# Revit family: Комби-клапан – регулятор расхода 4006_R
name_source: partatom
category: Rohrzubehör
revit_build: Autodesk Revit 2018 (Build: 20190510_1515(x64)
units: mm (PartAtom-declared; Revit-internal decimal feet)

## family parameters
Arbeitsebenenbasiert = Nein
Beim Laden mit Abzugskörper schneiden = Nein
Bemaßung runder Anschluss = Durchmesser verwenden
Gemeinsam genutzt = Nein
Immer vertikal = Ja
OmniClass-Nummer = 23.65.55.14
OmniClass-Titel = Valves for Liquid Services
Teiletyp = Unterbricht

## types (1)
- Комби-клапан – регулятор расхода 4006_R
    H05 = 9 mm  [stored 0.0295276 ft]
    H07 = 4 mm  [stored 0.0131234 ft]
    H09 = 21.8 mm  [stored 0.0715223 ft]
    H12 = 19.25 mm  [stored 0.0631562 ft]
    Hersteller = Herz-Armaturen GmbH
    L02 = 43.5 mm  [stored 0.142717 ft]
    L03 = 3.2 mm  [stored 0.0104987 ft]
    L04 = 1.5 mm  [stored 0.00492126 ft]
    L05 = 11 mm  [stored 0.0360892 ft]
    PN = 16
    R04 = 12.5 mm  [stored 0.0410105 ft]
    R05 = 15 mm  [stored 0.0492126 ft]
    R08 = 11.3 mm  [stored 0.0370735 ft]
    R09 = 18.25 mm  [stored 0.0598753 ft]
    R10 = 35 mm  [stored 0.114829 ft]
    R11 = 6.5 mm
    R12 = 3.9 mm  [stored 0.0127953 ft]
    SCRNCODE = 05;04;02
    SCRNSEQ = ARM;ARM_TYP="DURR";2
    URL = www.herz-armaturen.ru
    VRL02 = 18 mm  [stored 0.0590551 ft]
    VRL04 = 8 mm  [stored 0.0262467 ft]
    Защитный колпачок = Пластик
    Импульсная трубка = Медь Cu-DHP (CW024A)
    Кольцевое уплотнение O-Ring = EPDM
    Корпус = Латунь, устойчивая к селективной цинковой коррозии
    Корпус мембраны = латунь CW602N
    Макс. рабочая температура до DN32 = 130 °C
    Макс. рабочая температура от DN40 = 110 °C
    Макс. рабочее давление = 1600000.0 Pa
    Мембрана = EPDM
    Мин. рабочая температура (антифриз) = -20 °C
    Мин. рабочая температура (чистая вода) = 2 °C
    Область применения = Комби-клапан применяется в системах отопления и охлаждения с насосами. Комби-клапан автоматически ограничивает расход на выбранном участке системы до заданного значения, компенсируя все колебания давления. При этом нет необходимости в измерениях, а регулирование эффективно при любых условиях эксплуатации. Комби-клапан регулирует расход в соответствии с настройкой до заданного значения; на мембрану воздействует давление непосредственно до и после регулирующей части.
    Пружина = Пружинная нержавеющая сталь
    Среда = Качество теплоносителя в соответствии с ÖNORM H5195 и/или предписаниями VDI-Standard 2035.
Разрешается использование смеси этилен- или пропиленгликоля в соотношении 25-50% с водой.
    Ход = 4 mm  [stored 0.0131234 ft]
    Шпиндель = Нержавеющая сталь 14301

note: [stored X ft] marks values corroborated as IEEE doubles in the binary element streams (Revit-internal decimal feet)
